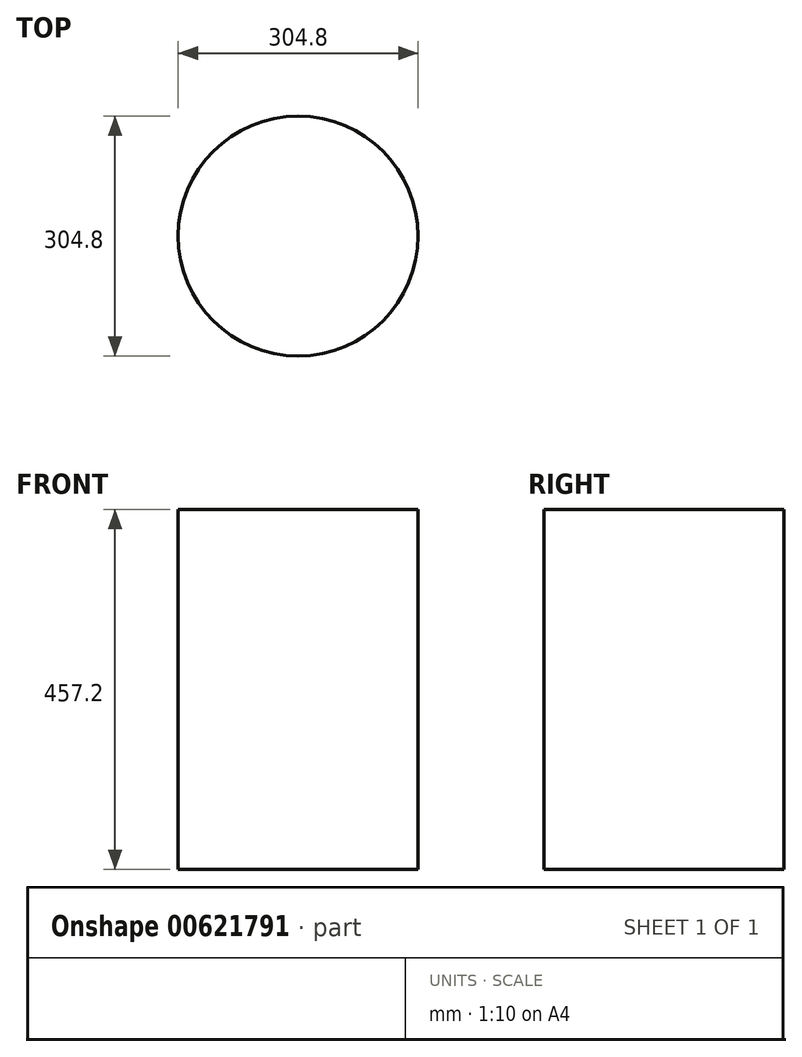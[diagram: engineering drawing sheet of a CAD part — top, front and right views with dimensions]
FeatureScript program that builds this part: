
annotation { "Feature Type Name" : "Feature", "Feature Type Description" : "" }
export const myFeature = defineFeature(function(context is Context, id is Id, definition is map)
    precondition{}
    {
        {
            var Q0;
            Q0=qCreatedBy(makeId("Front.planeOp"),FACE);
            var sketch = newSketch(context, id + "F0", { "sketchPlane" : qUnion([Q0])});
            skLineSegment(sketch, "E0.bottom", {"start": v(-152.4, -228.6) * mm, "end": v(152.4, -228.6) * mm});
            skLineSegment(sketch, "E0.top", {"start": v(-152.4, 228.6) * mm, "end": v(152.4, 228.6) * mm});
            skLineSegment(sketch, "E0.left", {"start": v(-152.4, -228.6) * mm, "end": v(-152.4, 228.6) * mm});
            skLineSegment(sketch, "E0.right", {"start": v(152.4, -228.6) * mm, "end": v(152.4, 228.6) * mm});
            skPoint(sketch, "E0.middle", {"position": v(0, 0) * mm});
            skLineSegment(sketch, "E1", {"start": v(0, 228.6) * mm, "end": v(0, -228.6) * mm, "construction": true});
            skPoint(sketch, "E1.endSnap0", {"position": v(0, -228.6) * mm});
            skLineSegment(sketch, "E2", {"start": v(-25.4, -355.6) * mm, "end": v(-25.4, -482.6) * mm});
            skLineSegment(sketch, "E3", {"start": v(-25.4, -482.6) * mm, "end": v(25.4, -482.6) * mm});
            skLineSegment(sketch, "E4", {"start": v(25.4, -482.6) * mm, "end": v(25.4, -355.6) * mm});
            skLineSegment(sketch, "E5", {"start": v(-152.4, -228.6) * mm, "end": v(-25.4, -355.6) * mm});
            skLineSegment(sketch, "E6", {"start": v(152.4, -228.6) * mm, "end": v(25.4, -355.6) * mm});
            skPoint(sketch, "E7.orphan", {"position": v(25.4, -228.6) * mm});
            skPoint(sketch, "E8.orphan", {"position": v(-25.4, -228.6) * mm});
            skPoint(sketch, "E9.end.orphan", {"position": v(0, -366.16) * mm});
            skLineSegment(sketch, "E10", {"start": v(0, -228.6) * mm, "end": v(0, -366.16) * mm, "construction": true});
            skLineSegment(sketch, "E11", {"start": v(0, -366.16) * mm, "end": v(0, -482.6) * mm, "construction": true});
            skSolve(sketch);
        }
        {
            var Q0;
            Q0=makeQuery(id+"F0.imprint","IMPRINT",FACE,{"disambiguationData":[TD([[makeQuery(id+"F0.imprint","IMPRINT",EDGE,{"derivedFrom":sQuery(id+"F0.wireOp",EDGE,"E0.bottom")}),1.0]])]});
            var Q1;
            Q1=makeQuery(id+"F0.imprint","IMPRINT",FACE,{"disambiguationData":[TD([[makeQuery(id+"F0.imprint","IMPRINT",EDGE,{"derivedFrom":sQuery(id+"F0.wireOp",EDGE,"E0.bottom")}),-1.0]])]});
            var Q2;
            Q2=sQuery(id+"F0.wireOp",EDGE,"E0.left");
            var Q3;
            Q3=sQuery(id+"F0.wireOp",EDGE,"E1");
            revolve(context, id + "F1", {"bodyType" : ToolBodyType.SURFACE, "entities" : qUnion([Q0, Q1]), "surfaceEntities" : qUnion([Q2]), "axis" : qUnion([Q3]), "revolveType" : RevolveType.FULL});
        }
    });
